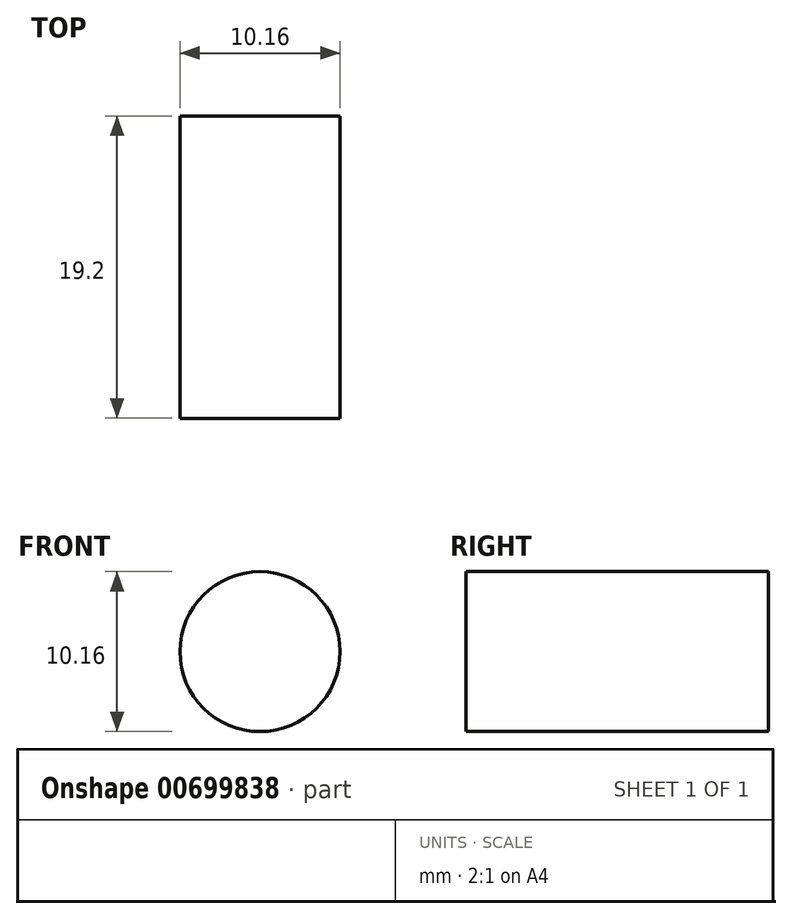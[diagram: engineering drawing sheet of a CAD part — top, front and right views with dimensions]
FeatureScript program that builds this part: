
annotation { "Feature Type Name" : "Feature", "Feature Type Description" : "" }
export const myFeature = defineFeature(function(context is Context, id is Id, definition is map)
    precondition{}
    {
        {
            var Q0;
            Q0=qCreatedBy(makeId("Front.planeOp"),FACE);
            var sketch = newSketch(context, id + "F0", { "sketchPlane" : qUnion([Q0])});
            skCircle(sketch, "E0", {"center": v(0, 0) * mm, "radius": 5.08 * mm});
            skSolve(sketch);
        }
        {
            var Q0;
            Q0=makeQuery(id+"F0.imprint","IMPRINT",FACE,{"disambiguationData":[TD([[makeQuery(id+"F0.imprint","IMPRINT",EDGE,{"derivedFrom":sQuery(id+"F0.wireOp",EDGE,"E0")}),1.0]])]});
            extrude(context, id + "F1", {"entities" : qUnion([Q0]), "depth" : 19.2 * mm});
        }
    });
